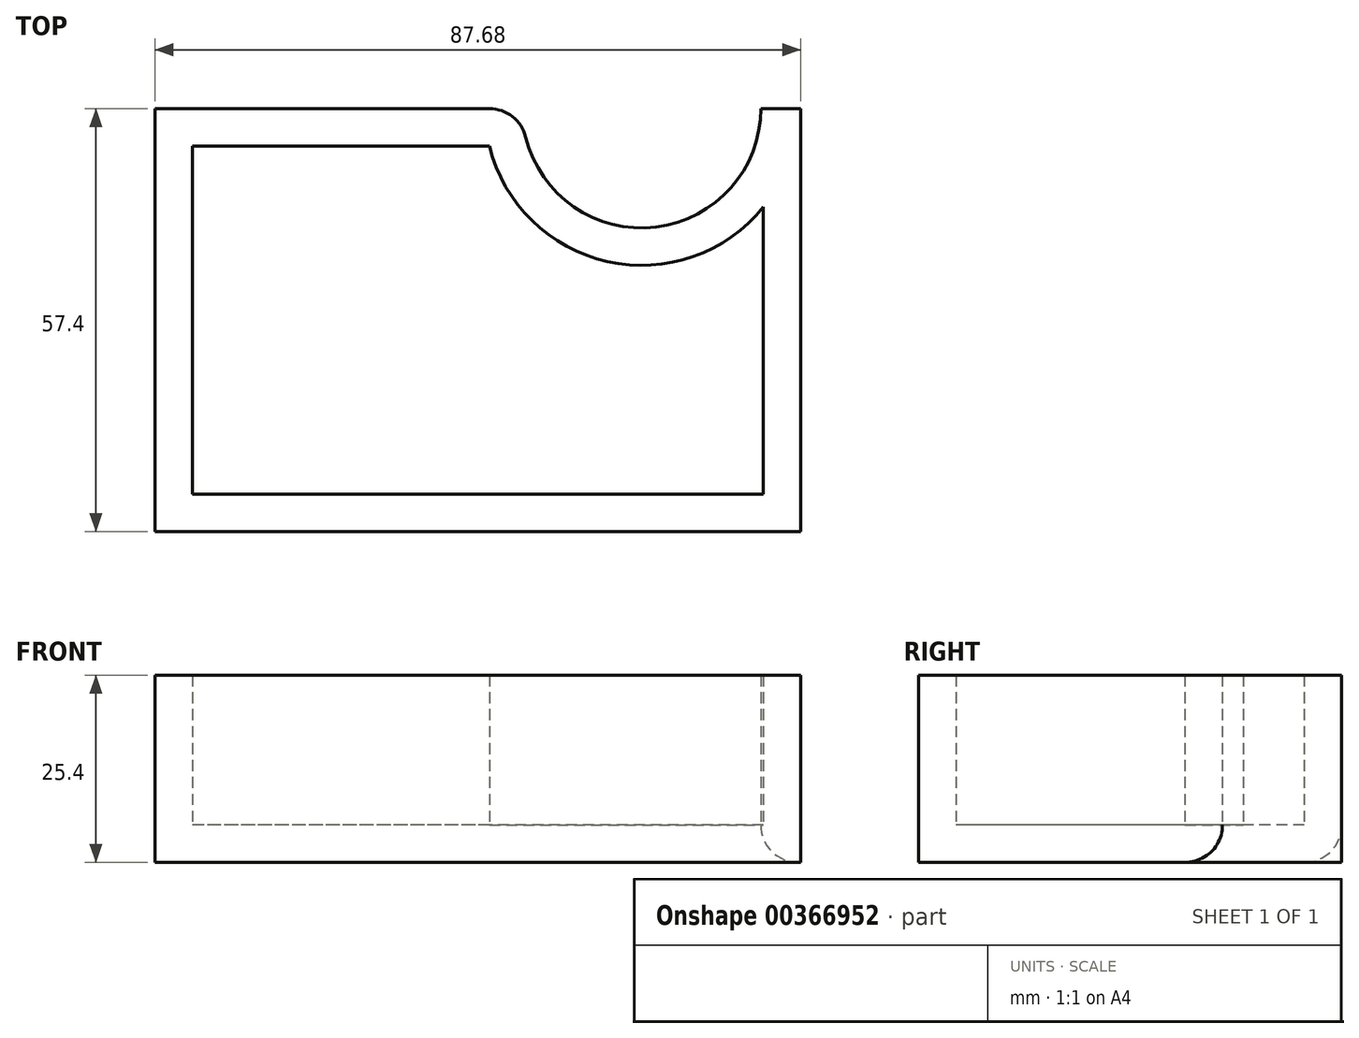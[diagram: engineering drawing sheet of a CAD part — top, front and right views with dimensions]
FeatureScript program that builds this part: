
annotation { "Feature Type Name" : "Feature", "Feature Type Description" : "" }
export const myFeature = defineFeature(function(context is Context, id is Id, definition is map)
    precondition{}
    {
        {
            var Q0;
            Q0=qCreatedBy(makeId("Top.planeOp"),FACE);
            var sketch = newSketch(context, id + "F0", { "sketchPlane" : qUnion([Q0])});
            skLineSegment(sketch, "E0.bottom", {"start": v(43.84, 28.7) * mm, "end": v(38.4, 28.7) * mm});
            skLineSegment(sketch, "E0.top", {"start": v(43.84, -28.7) * mm, "end": v(-43.84, -28.7) * mm});
            skLineSegment(sketch, "E0.left", {"start": v(43.84, 28.7) * mm, "end": v(43.84, -28.7) * mm});
            skLineSegment(sketch, "E0.right", {"start": v(-43.84, 28.7) * mm, "end": v(-43.84, -28.7) * mm});
            skPoint(sketch, "E0.middle", {"position": v(0, 0) * mm});
            skArc(sketch, "E1", {"start": v(6.03, 28.7) * mm, "mid": v(22.21, 12.52) * mm, "end": v(38.4, 28.7) * mm});
            skLineSegment(sketch, "E2.trimOffspring", {"start": v(6.03, 28.7) * mm, "end": v(-43.84, 28.7) * mm});
            skSolve(sketch);
        }
        {
            var Q0;
            Q0 = qSketchRegion(id + "F0", true);
            extrude(context, id + "F1", {"entities" : qUnion([Q0]), "depth" : 25.4 * mm});
        }
        {
            var Q0;
            Q0=makeQuery(id+"F1.opExtrude","CAP_EDGE",EDGE,{"disambiguationData":[OSD([sQuery(id+"F0.wireOp",EDGE,"E2.trimOffspring")])],"isStart":true});
            var Q1;
            Q1=makeQuery(id+"F1.opExtrude","CAP_EDGE",EDGE,{"disambiguationData":[OSD([sQuery(id+"F0.wireOp",EDGE,"E1")])],"isStart":true});
            var Q2;
            Q2=makeQuery(id+"F1.opExtrude","SWEPT_EDGE",EDGE,{"disambiguationData":[OSD([sQuery(id+"F0.wireOp",EDGE,"E1"),sQuery(id+"F0.wireOp",EDGE,"E2.trimOffspring")])]});
            fillet(context, id + "F2", {"entities" : qUnion([Q0, Q1, Q2]), "radius" : 5.08 * mm, "tangentPropagation" : true, "allowEdgeOverflow" : false});
        }
        {
            var Q0;
            Q0=makeQuery(id+"F1.opExtrude","CAP_FACE",FACE,{"disambiguationData":[OSD([sQuery(id+"F0.wireOp",EDGE,"E0.bottom"),sQuery(id+"F0.wireOp",EDGE,"E0.top"),sQuery(id+"F0.wireOp",EDGE,"E0.left"),sQuery(id+"F0.wireOp",EDGE,"E0.right"),sQuery(id+"F0.wireOp",EDGE,"E1"),sQuery(id+"F0.wireOp",EDGE,"E2.trimOffspring")])],"isStart":false});
            shell(context, id + "F3", {"entities" : qUnion([Q0]), "thickness" : 5.08 * mm});
        }
    });
